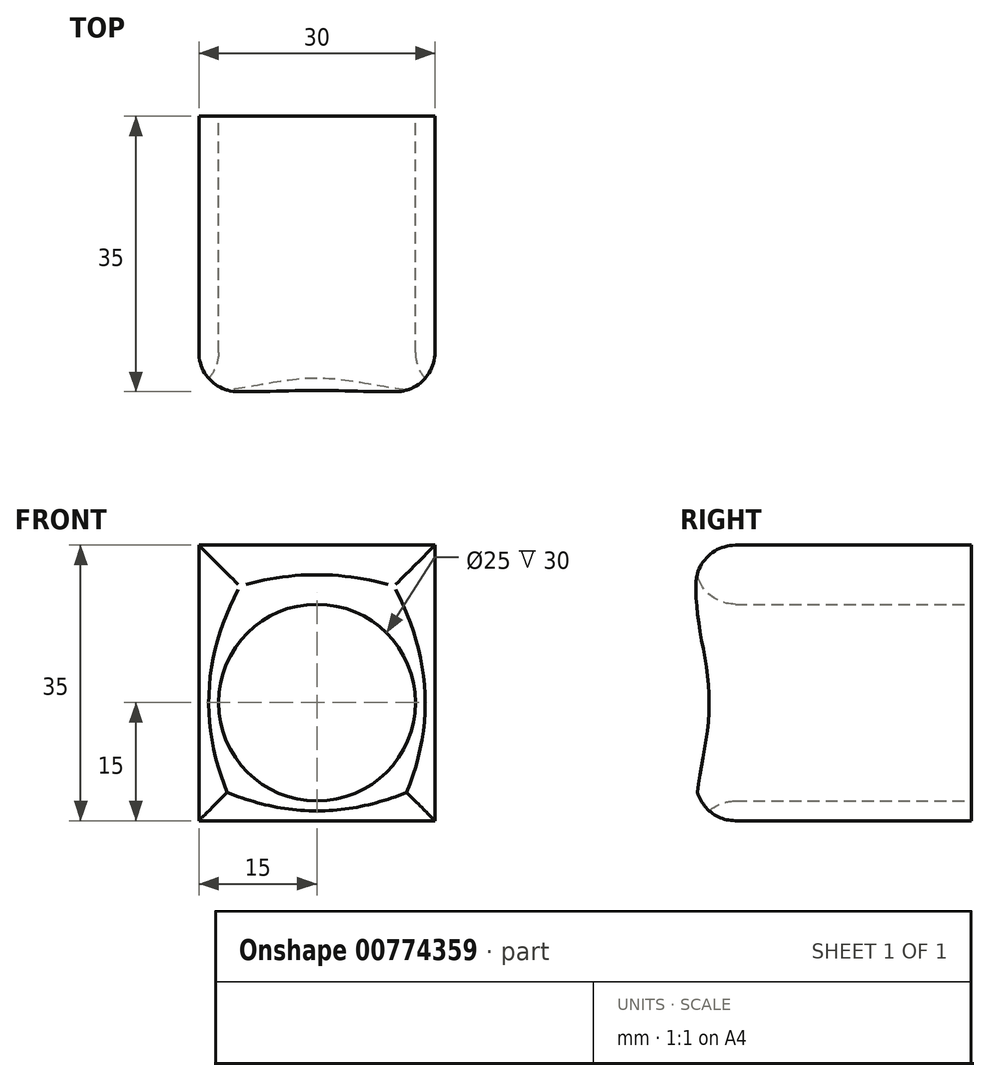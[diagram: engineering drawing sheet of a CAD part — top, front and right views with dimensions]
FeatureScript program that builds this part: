
annotation { "Feature Type Name" : "Feature", "Feature Type Description" : "" }
export const myFeature = defineFeature(function(context is Context, id is Id, definition is map)
    precondition{}
    {
        {
            var Q0;
            Q0=qCreatedBy(makeId("Front.planeOp"),FACE);
            var sketch = newSketch(context, id + "F0", { "sketchPlane" : qUnion([Q0])});
            skLineSegment(sketch, "E0.bottom", {"start": v(-15, 15) * mm, "end": v(15, 15) * mm});
            skLineSegment(sketch, "E0.top", {"start": v(-15, -15) * mm, "end": v(15, -15) * mm});
            skLineSegment(sketch, "E0.left", {"start": v(-15, 15) * mm, "end": v(-15, -15) * mm});
            skLineSegment(sketch, "E0.right", {"start": v(15, 15) * mm, "end": v(15, -15) * mm});
            skCircle(sketch, "E1", {"center": v(0, 0) * mm, "radius": 12.5 * mm});
            skSolve(sketch);
        }
        {
            var Q0;
            Q0 = qSketchRegion(id + "F0", true);
            extrude(context, id + "F1", {"entities" : qUnion([Q0]), "endBound" : BoundingType.SYMMETRIC, "depth" : 35 * mm, "offsetDistance" : 25 * mm});
        }
        {
            var Q0;
            Q0=makeQuery(id+"F1.opExtrude","SWEPT_FACE",FACE,{"disambiguationData":[OSD([sQuery(id+"F0.wireOp",EDGE,"E0.bottom")])]});
            extrude(context, id + "F2", {"entities" : qUnion([Q0]), "operationType" : NewBodyOperationType.ADD, "depth" : 5 * mm, "offsetDistance" : 25 * mm});
        }
        {
            var Q0;
            {var subQ0=sQuery(id+"F0.wireOp",EDGE,"E0.bottom");Q0=makeQuery(id+"F2.boolean.opBoolean","MERGE",FACE,{"derivedFrom":[makeQuery(id+"F1.opExtrude","CAP_FACE",FACE,{"disambiguationData":[OSD([subQ0,sQuery(id+"F0.wireOp",EDGE,"E0.top"),sQuery(id+"F0.wireOp",EDGE,"E0.left"),sQuery(id+"F0.wireOp",EDGE,"E0.right"),sQuery(id+"F0.wireOp",EDGE,"E1")])],"isStart":false}),makeQuery(id+"F2.opExtrude","SWEPT_FACE",FACE,{"disambiguationData":[OSD([subQ0]),TDD([makeQuery(id+"F1.opExtrude","CAP_EDGE",EDGE,{"disambiguationData":[OSD([subQ0])],"isStart":false})])]})]});}
            var Q1;
            {var subQ0=sQuery(id+"F0.wireOp",EDGE,"E0.bottom");Q1=makeQuery(id+"F2.opExtrude","CAP_EDGE",EDGE,{"disambiguationData":[OSD([subQ0]),TDD([makeQuery(id+"F1.opExtrude","CAP_EDGE",EDGE,{"disambiguationData":[OSD([subQ0])],"isStart":false})])],"isStart":false});}
            fillet(context, id + "F3", {"entities" : qUnion([Q0, Q1]), "radius" : 5 * mm, "allowEdgeOverflow" : false});
        }
    });
